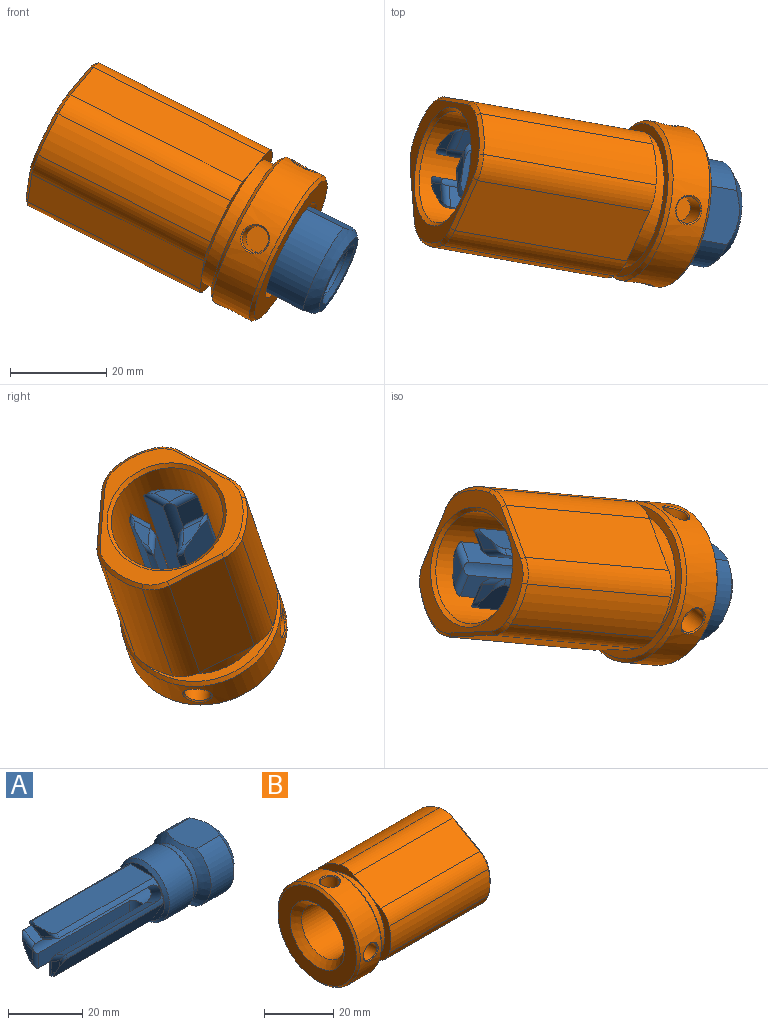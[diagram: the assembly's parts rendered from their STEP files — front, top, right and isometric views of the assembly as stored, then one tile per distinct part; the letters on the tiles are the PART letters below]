
ASSEMBLY  parts=2 mates=1
PART A: 49 faces, bbox 64.6x22.2x22.2 mm
  f0: plane 5.77x3.33mm, normal (-1,0,0), area 10.2mm2, adj f7,f13,f45,f46
  f1: cylinder r=3.81mm len=47.82mm, axis (1,0,0), area 563.6mm2, adj f23,f34,f35,f36,f37,f38,f39,f40
  f2: torus R=6.99mm, axis (-1,0,0), area 3.6mm2, adj f4,f14,f31,f44
  f3: cylinder r=8.26mm len=36.83mm, axis (1,0,0), area 59.8mm2, adj f13,f21,f32,f38,f40
  f4: plane 5.77x3.33mm, normal (-1,0,0), area 10.2mm2, adj f2,f11,f43,f44
  f5: torus R=6.99mm, axis (-1,0,0), area 3.6mm2, adj f9,f22,f33,f48
  f6: cylinder r=8.26mm len=36.83mm, axis (1,0,0), area 59.8mm2, adj f11,f21,f31,f36,f41
  f7: torus R=6.99mm, axis (-1,0,0), area 3.6mm2, adj f0,f12,f32,f45
  f8: cylinder r=8.26mm len=36.83mm, axis (1,0,0), area 59.8mm2, adj f10,f21,f33,f34,f42
  f9: plane 6.66x2.77mm, normal (-1,0,0), area 10.2mm2, adj f5,f10,f47,f48
  f10: torus R=6.99mm, axis (-1,0,0), area 3.6mm2, adj f8,f9,f33,f47
  f11: torus R=6.99mm, axis (-1,0,0), area 3.6mm2, adj f4,f6,f31,f43
  f12: cylinder r=8.26mm len=36.83mm, axis (1,0,0), area 59.8mm2, adj f7,f21,f32,f35,f42
  f13: torus R=6.99mm, axis (-1,0,0), area 3.6mm2, adj f0,f3,f32,f46
  f14: cylinder r=8.26mm len=36.83mm, axis (1,0,0), area 59.8mm2, adj f2,f21,f31,f39,f40
  f15: cylinder r=11.11mm len=19.05mm, axis (1,0,0), area 199.5mm2, adj f17,f18,f27,f28
  f16: cylinder r=11.11mm len=19.05mm, axis (1,0,0), area 199.5mm2, adj f17,f18,f27,f28
  f17: cone r=8.57mm half-angle=45deg, axis (1,0,0), area 187.4mm2, adj f15,f16,f19,f27,f28
  f18: cone r=8.57mm half-angle=45deg, axis (-1,0,0), area 187.4mm2, adj f15,f16,f26,f27,f28
  f19: cylinder r=8.57mm len=17.15mm, axis (1,0,0), area 85.5mm2, adj f17,f30
  f20: cylinder r=9.53mm len=19.05mm, axis (1,0,0), area 550.3mm2, adj f29,f30
  f21: plane 17.12x17.12mm, normal (-1,0,0), area 38.8mm2, adj f3,f6,f8,f12,f14,f22,f29,f31
  f22: cylinder r=8.26mm len=36.83mm, axis (1,0,0), area 59.8mm2, adj f5,f21,f33,f37,f41
  f23: plane 11.79x11.79mm, normal (1,0,0), area 63.5mm2, adj f1,f24
  f24: cylinder r=5.89mm len=15.71mm, axis (1,0,0), area 581.6mm2, adj f23,f25
  f25: cone r=5.89mm half-angle=45deg, axis (1,0,0), area 57.8mm2, adj f24,f26
  f26: plane 17.15x17.15mm, normal (1,0,0), area 80.9mm2, adj f18,f25
  f27: plane 11.91x11.46mm, normal (0,0,1), area 123.6mm2, adj f15,f16,f17,f18
  f28: plane 11.91x11.46mm, normal (0,0,-1), area 123.6mm2, adj f15,f16,f17,f18
  f29: cone r=9.53mm half-angle=45deg, axis (1,0,0), area 77.6mm2, adj f20,f21
  f30: cone r=8.56mm half-angle=45deg, axis (-1,0,0), area 76.6mm2, adj f19,f20
  f31: plane 38.1x7.62mm, normal (0,-0.87,-0.5), area 333.8mm2, adj f2,f6,f11,f14,f21
  f32: plane 38.1x7.62mm, normal (0,0.87,-0.5), area 333.8mm2, adj f3,f7,f12,f13,f21
  f33: plane 38.1x8.8mm, normal (0,0,1), area 333.8mm2, adj f5,f8,f10,f21,f22
  f34: plane 34.45x4.27mm, normal (0,0.5,-0.87), area 169.8mm2, adj f1,f8,f42,f47
  f35: plane 34.45x4.27mm, normal (0,-0.5,0.87), area 169.8mm2, adj f1,f12,f42,f45
  f36: plane 34.45x4.27mm, normal (0,0.5,0.87), area 169.8mm2, adj f1,f6,f41,f43
  f37: plane 34.45x4.27mm, normal (0,-0.5,-0.87), area 169.8mm2, adj f1,f22,f41,f48
  f38: plane 34.45x4.93mm, normal (0,-1,0), area 169.8mm2, adj f1,f3,f40,f46
  f39: plane 34.45x4.93mm, normal (0,1,0), area 169.8mm2, adj f1,f14,f40,f44
  f40: cylinder r=2.38mm len=5.28mm, axis (0,0,-1), area 35.1mm2, adj f1,f3,f14,f38,f39
  f41: cylinder r=2.38mm len=6.95mm, axis (0,-0.87,0.5), area 35.1mm2, adj f1,f6,f22,f36,f37
  f42: cylinder r=2.38mm len=6.95mm, axis (0,-0.87,-0.5), area 35.1mm2, adj f1,f8,f12,f34,f35
  f43: cylinder r=1.27mm len=5.83mm, axis (0,0.87,-0.5), area 9.4mm2, adj f1,f4,f11,f36,f44
  f44: cylinder r=1.27mm len=6mm, axis (0,0,-1), area 9.4mm2, adj f1,f2,f4,f39,f43
  f45: cylinder r=1.27mm len=5.83mm, axis (0,0.87,0.5), area 9.4mm2, adj f0,f1,f7,f35,f46
  f46: cylinder r=1.27mm len=6mm, axis (0,0,1), area 9.4mm2, adj f0,f1,f13,f38,f45
  f47: cylinder r=1.27mm len=5.83mm, axis (0,-0.87,-0.5), area 9.4mm2, adj f1,f9,f10,f34,f48
  f48: cylinder r=1.27mm len=5.83mm, axis (0,-0.87,0.5), area 9.4mm2, adj f1,f5,f9,f37,f47
PART B: 52 faces, bbox 54.6x33.7x33.7 mm
  f0: cylinder r=2.8mm len=5.59mm, axis (0,1,0), area 84.8mm2, adj f1,f48
  f1: plane 5.59x5.59mm, normal (0,1,0), area 24.6mm2, adj f0
  f2: cylinder r=2.8mm len=5.59mm, axis (0,0,-1), area 84.8mm2, adj f3,f51
  f3: plane 5.59x5.59mm, normal (0,0,-1), area 24.6mm2, adj f2
  f4: cylinder r=2.8mm len=5.59mm, axis (0,-1,0), area 84.8mm2, adj f5,f50
  f5: plane 5.59x5.59mm, normal (0,-1,0), area 24.6mm2, adj f4
  f6: cylinder r=16.83mm len=40.51mm, axis (-1,0,0), area 390.2mm2, adj f17,f26,f29,f38
  f7: cylinder r=16.83mm len=40.51mm, axis (-1,0,0), area 390.2mm2, adj f8,f25,f28,f37
  f8: plane 21.43x16.57mm, normal (-1,0,0), area 50.6mm2, adj f7,f18,f23,f24,f25,f28
  f9: plane 21.43x16.57mm, normal (-1,0,0), area 50.6mm2, adj f16,f18,f22,f23,f27,f30
  f10: cone r=11.11mm half-angle=45deg, axis (-1,0,0), area 208.5mm2, adj f11,f21
  f11: cylinder r=8.75mm len=17.5mm, axis (-1,0,0), area 638.2mm2, adj f10,f12
  f12: plane 18.42x18.42mm, normal (1,0,0), area 25.8mm2, adj f11,f13
  f13: torus R=9.21mm, axis (-1,0,0), area 271.4mm2, adj f12,f14
  f14: cylinder r=11.75mm len=37.34mm, axis (-1,0,0), area 2756mm2, adj f13,f33
  f15: plane 31.61x29.59mm, normal (1,0,0), area 225.7mm2, adj f33,f34,f35,f36,f37,f38,f39,f40
  f16: cylinder r=16.83mm len=40.51mm, axis (-1,0,0), area 390.2mm2, adj f9,f27,f30,f45
  f17: plane 24.75x9.68mm, normal (-1,0,0), area 50.6mm2, adj f6,f18,f22,f24,f26,f29
  f18: cylinder r=14.29mm len=28.58mm, axis (-1,0,0), area 285mm2, adj f8,f9,f17,f19
  f19: plane 32.13x32.13mm, normal (1,0,0), area 169.5mm2, adj f18,f31
  f20: cylinder r=16.83mm len=33.66mm, axis (-1,0,0), area 794mm2, adj f31,f32,f48,f49,f50,f51
  f21: plane 32.13x32.13mm, normal (-1,0,0), area 422.9mm2, adj f10,f32
  f22: plane 40.51x11mm, normal (0,-0.5,-0.87), area 514.5mm2, adj f9,f17,f29,f30,f42
  f23: plane 40.51x12.7mm, normal (0,1,0), area 514.5mm2, adj f8,f9,f27,f28,f41
  f24: plane 40.51x11mm, normal (0,-0.5,0.87), area 514.5mm2, adj f8,f17,f25,f26,f34
  f25: cylinder r=7.62mm len=40.51mm, axis (-1,0,0), area 234.9mm2, adj f7,f8,f24,f35
  f26: cylinder r=7.62mm len=40.51mm, axis (-1,0,0), area 234.9mm2, adj f6,f17,f24,f36
  f27: cylinder r=7.62mm len=40.51mm, axis (-1,0,0), area 234.9mm2, adj f9,f16,f23,f43
  f28: cylinder r=7.62mm len=40.51mm, axis (-1,0,0), area 234.9mm2, adj f7,f8,f23,f39
  f29: cylinder r=7.62mm len=40.51mm, axis (-1,0,0), area 234.9mm2, adj f6,f17,f22,f40
  f30: cylinder r=7.62mm len=40.51mm, axis (-1,0,0), area 234.9mm2, adj f9,f16,f22,f44
  f31: cone r=16.83mm half-angle=45deg, axis (-1,0,0), area 111.4mm2, adj f19,f20
  f32: cone r=16.07mm half-angle=45deg, axis (1,0,0), area 111.4mm2, adj f20,f21
  f33: cone r=12.51mm half-angle=45deg, axis (1,0,0), area 82.1mm2, adj f14,f15
  f34: plane 11.38x7.01mm, normal (0.71,-0.35,0.61), area 13.7mm2, adj f15,f24,f35,f36
  f35: cone r=6.86mm half-angle=45deg, axis (-1,0,0), area 5.9mm2, adj f15,f25,f34,f37
  f36: cone r=6.86mm half-angle=45deg, axis (-1,0,0), area 5.9mm2, adj f15,f26,f34,f38
  f37: cone r=16.83mm half-angle=45deg, axis (-1,0,0), area 10.1mm2, adj f7,f15,f35,f39
  f38: cone r=16.83mm half-angle=45deg, axis (-1,0,0), area 10.1mm2, adj f6,f15,f36,f40
  f39: cone r=6.86mm half-angle=45deg, axis (-1,0,0), area 5.9mm2, adj f15,f28,f37,f41
  f40: cone r=6.86mm half-angle=45deg, axis (-1,0,0), area 5.9mm2, adj f15,f29,f38,f42
  f41: plane 12.7x0.76mm, normal (0.71,0.71,0), area 13.7mm2, adj f15,f23,f39,f43
  f42: plane 11.38x7.01mm, normal (0.71,-0.35,-0.61), area 13.7mm2, adj f15,f22,f40,f44
  f43: cone r=6.86mm half-angle=45deg, axis (-1,0,0), area 5.9mm2, adj f15,f27,f41,f45
  f44: cone r=6.86mm half-angle=45deg, axis (-1,0,0), area 5.9mm2, adj f15,f30,f42,f45
  f45: cone r=16.83mm half-angle=45deg, axis (-1,0,0), area 10.1mm2, adj f15,f16,f43,f44
  f46: cylinder r=2.8mm len=5.59mm, axis (0,0,1), area 84.8mm2, adj f47,f49
  f47: plane 5.59x5.59mm, normal (0,0,1), area 24.6mm2, adj f46
  f48: bspline ~6.19x6.09mm, area 6.9mm2, adj f0,f20
  f49: bspline ~6.19x6.09mm, area 6.9mm2, adj f20,f46
  f50: bspline ~6.19x6.09mm, area 6.9mm2, adj f4,f20
  f51: bspline ~6.19x6.09mm, area 6.9mm2, adj f2,f20
PLACE A rot(axis=(0.08,0.93,-0.35),28.2deg) t=(151.23,38.08,28.79)mm
PLACE B rot(axis=(-0.09,-1,-0.02),153.7deg) t=(92.8,48.38,58.34)mm
MATE planar A.f1 <-> B.f6  axis (0.88,-0.16,-0.45) through (140.93,39.9,33.99)mm
